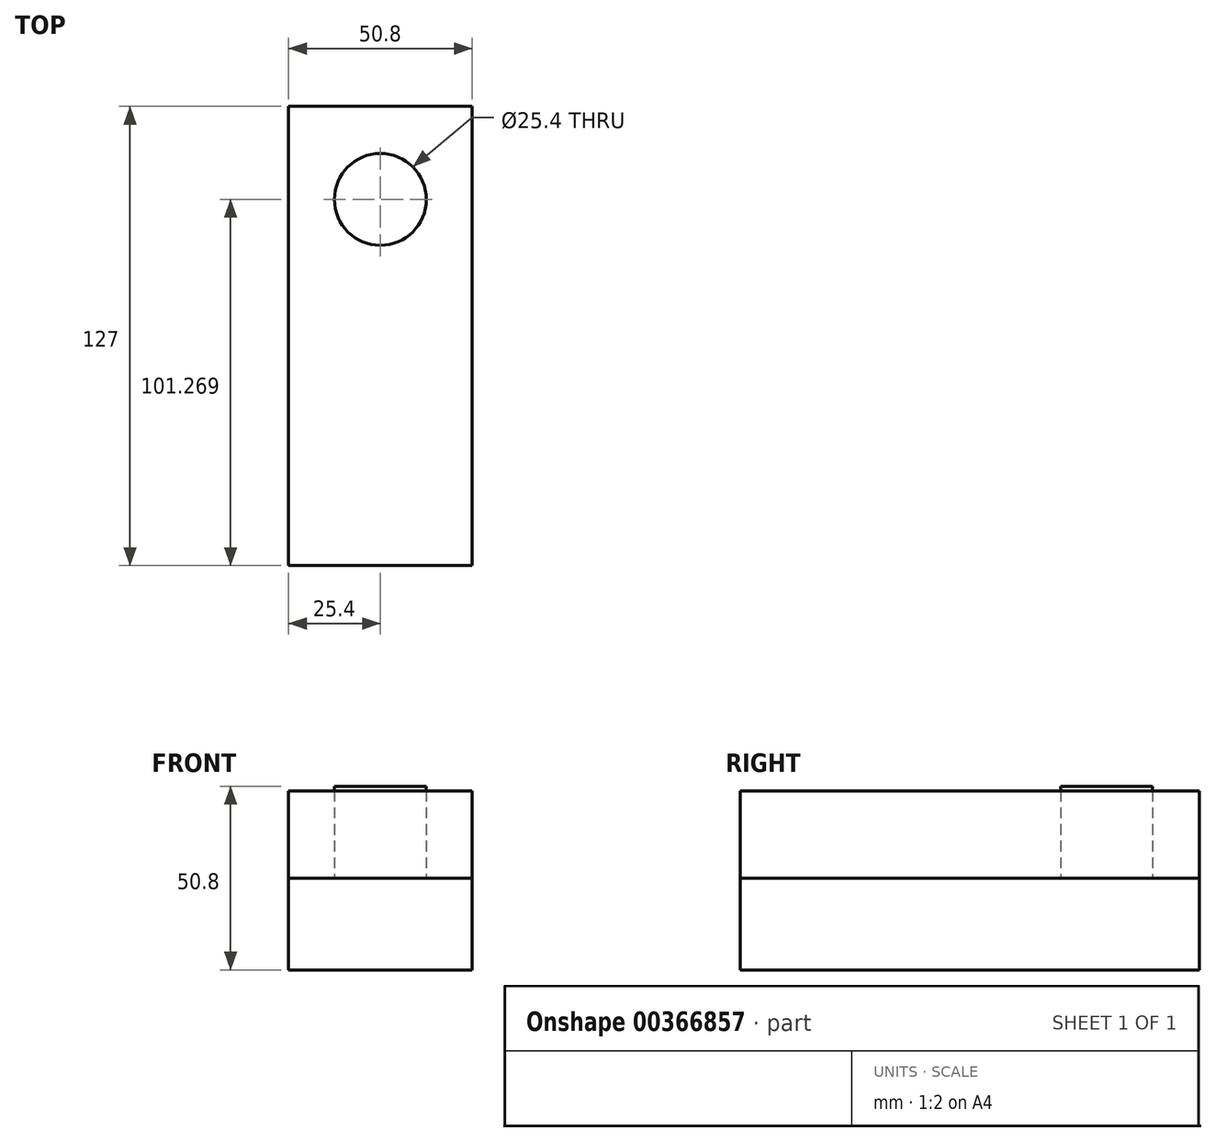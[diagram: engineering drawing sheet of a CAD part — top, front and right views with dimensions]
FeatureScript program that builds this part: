
annotation { "Feature Type Name" : "Feature", "Feature Type Description" : "" }
export const myFeature = defineFeature(function(context is Context, id is Id, definition is map)
    precondition{}
    {
        {
            var Q0;
            Q0=qCreatedBy(makeId("Top.planeOp"),FACE);
            var sketch = newSketch(context, id + "F0", { "sketchPlane" : qUnion([Q0])});
            skLineSegment(sketch, "E0.bottom", {"start": v(-25.4, -63.5) * mm, "end": v(25.4, -63.5) * mm});
            skLineSegment(sketch, "E0.top", {"start": v(-25.4, 63.5) * mm, "end": v(25.4, 63.5) * mm});
            skLineSegment(sketch, "E0.left", {"start": v(-25.4, -63.5) * mm, "end": v(-25.4, 63.5) * mm});
            skLineSegment(sketch, "E0.right", {"start": v(25.4, -63.5) * mm, "end": v(25.4, 63.5) * mm});
            skPoint(sketch, "E1", {"position": v(-25.4, 0) * mm});
            skPoint(sketch, "E2", {"position": v(0, 63.5) * mm});
            skPoint(sketch, "E3", {"position": v(25.4, 0) * mm});
            skPoint(sketch, "E4", {"position": v(0, -63.5) * mm});
            skSolve(sketch);
        }
        {
            var Q0;
            Q0 = qSketchRegion(id + "F0", true);
            extrude(context, id + "F1", {"entities" : qUnion([Q0]), "depth" : 25.4 * mm});
        }
        {
            var Q0;
            Q0=makeQuery(id+"F1.opExtrude","CAP_FACE",FACE,{"disambiguationData":[OSD([sQuery(id+"F0.wireOp",EDGE,"E0.bottom"),sQuery(id+"F0.wireOp",EDGE,"E0.top"),sQuery(id+"F0.wireOp",EDGE,"E0.left"),sQuery(id+"F0.wireOp",EDGE,"E0.right")])],"isStart":false});
            var sketch = newSketch(context, id + "F2", { "sketchPlane" : qUnion([Q0])});
            skCircle(sketch, "E5", {"center": v(0, 37.77) * mm, "radius": 12.7 * mm});
            skSolve(sketch);
        }
        {
            var Q0;
            Q0 = qSketchRegion(id + "F2", true);
            extrude(context, id + "F3", {"entities" : qUnion([Q0]), "operationType" : NewBodyOperationType.ADD, "depth" : 25.4 * mm});
        }
        {
            var Q0;
            Q0=makeQuery(id+"F1.opExtrude","CAP_FACE",FACE,{"disambiguationData":[OSD([sQuery(id+"F0.wireOp",EDGE,"E0.bottom"),sQuery(id+"F0.wireOp",EDGE,"E0.top"),sQuery(id+"F0.wireOp",EDGE,"E0.left"),sQuery(id+"F0.wireOp",EDGE,"E0.right")])],"isStart":false});
            var sketch = newSketch(context, id + "F4", { "sketchPlane" : qUnion([Q0])});
            skLineSegment(sketch, "E6.bottom", {"start": v(-25.4, -63.5) * mm, "end": v(25.4, -63.5) * mm});
            skLineSegment(sketch, "E6.top", {"start": v(-25.4, 63.5) * mm, "end": v(25.4, 63.5) * mm});
            skLineSegment(sketch, "E6.left", {"start": v(-25.4, -63.5) * mm, "end": v(-25.4, 63.5) * mm});
            skLineSegment(sketch, "E6.right", {"start": v(25.4, -63.5) * mm, "end": v(25.4, 63.5) * mm});
            skCircle(sketch, "E7.0", {"center": v(0, 37.77) * mm, "radius": 12.7 * mm});
            skSolve(sketch);
        }
        {
            var Q0;
            Q0 = qSketchRegion(id + "F4", true);
            extrude(context, id + "F5", {"entities" : qUnion([Q0]), "depth" : 24.13 * mm});
        }
    });
